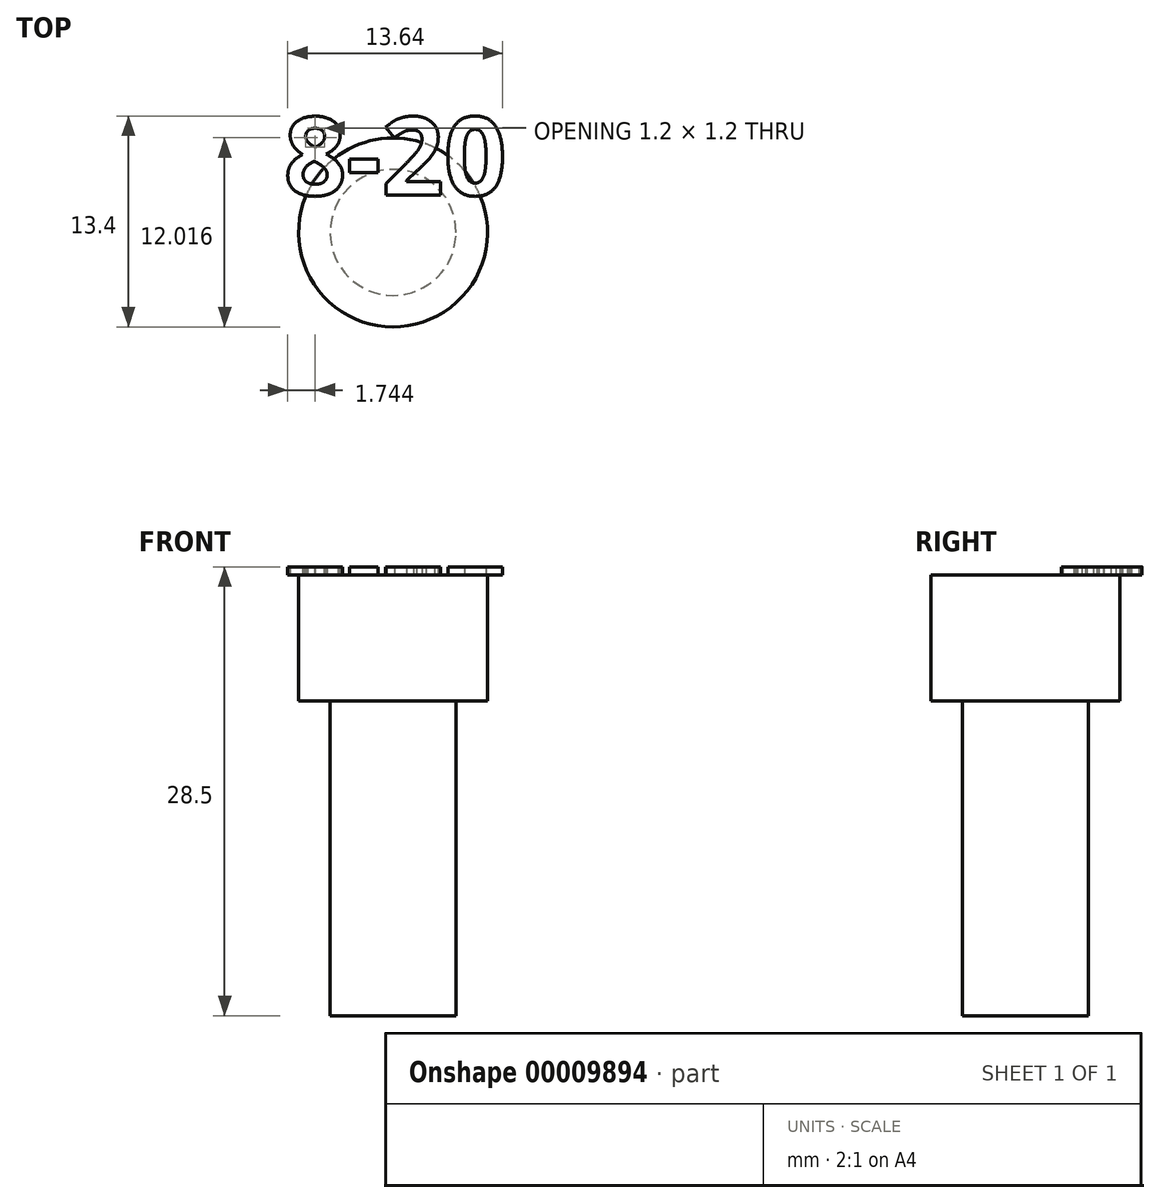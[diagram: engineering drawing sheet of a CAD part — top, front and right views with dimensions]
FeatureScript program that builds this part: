
annotation { "Feature Type Name" : "Feature", "Feature Type Description" : "" }
export const myFeature = defineFeature(function(context is Context, id is Id, definition is map)
    precondition{}
    {
        {
            var Q0;
            Q0=qCreatedBy(makeId("Top.planeOp"),FACE);
            var sketch = newSketch(context, id + "F0", { "sketchPlane" : qUnion([Q0])});
            skCircle(sketch, "E0", {"center": v(0, 0) * mm, "radius": 4 * mm});
            skSolve(sketch);
        }
        {
            var Q0;
            Q0 = qSketchRegion(id + "F0", true);
            extrude(context, id + "F1", {"entities" : qUnion([Q0]), "depth" : 20 * mm});
        }
        {
            var Q0;
            Q0=makeQuery(id+"F1.opExtrude","CAP_FACE",FACE,{"disambiguationData":[OSD([sQuery(id+"F0.wireOp",EDGE,"E0")])],"isStart":false});
            var sketch = newSketch(context, id + "F2", { "sketchPlane" : qUnion([Q0])});
            skCircle(sketch, "E1", {"center": v(0, 0) * mm, "radius": 6 * mm});
            skSolve(sketch);
        }
        {
            var Q0;
            Q0 = qSketchRegion(id + "F2", true);
            extrude(context, id + "F3", {"entities" : qUnion([Q0]), "operationType" : NewBodyOperationType.ADD, "depth" : 8 * mm});
        }
        {
            var Q0;
            Q0=makeQuery(id+"F3.opExtrude","CAP_FACE",FACE,{"disambiguationData":[OSD([sQuery(id+"F2.wireOp",EDGE,"E1")])],"isStart":false});
            var sketch = newSketch(context, id + "F4", { "sketchPlane" : qUnion([Q0]), "asVersion" : FeatureScriptVersionNumber.V307_HOLE_FEATURE_FIX_UNDETERMINED_TARGET_BODY_2});
            skText(sketch, "E2", { "text": "8-20", "fontName": "OpenSans-Bold.ttf"});
            const initialGuessF4  = {"E2": [-0.00693, 0.00236, 1, 0, 0.005]};
            skSetInitialGuess(sketch, initialGuessF4);
            skSolve(sketch);
        }
        {
            var Q0;
            Q0 = qSketchRegion(id + "F4", true);
            extrude(context, id + "F5", {"entities" : qUnion([Q0]), "operationType" : NewBodyOperationType.ADD, "depth" : 0.5 * mm});
        }
    });
